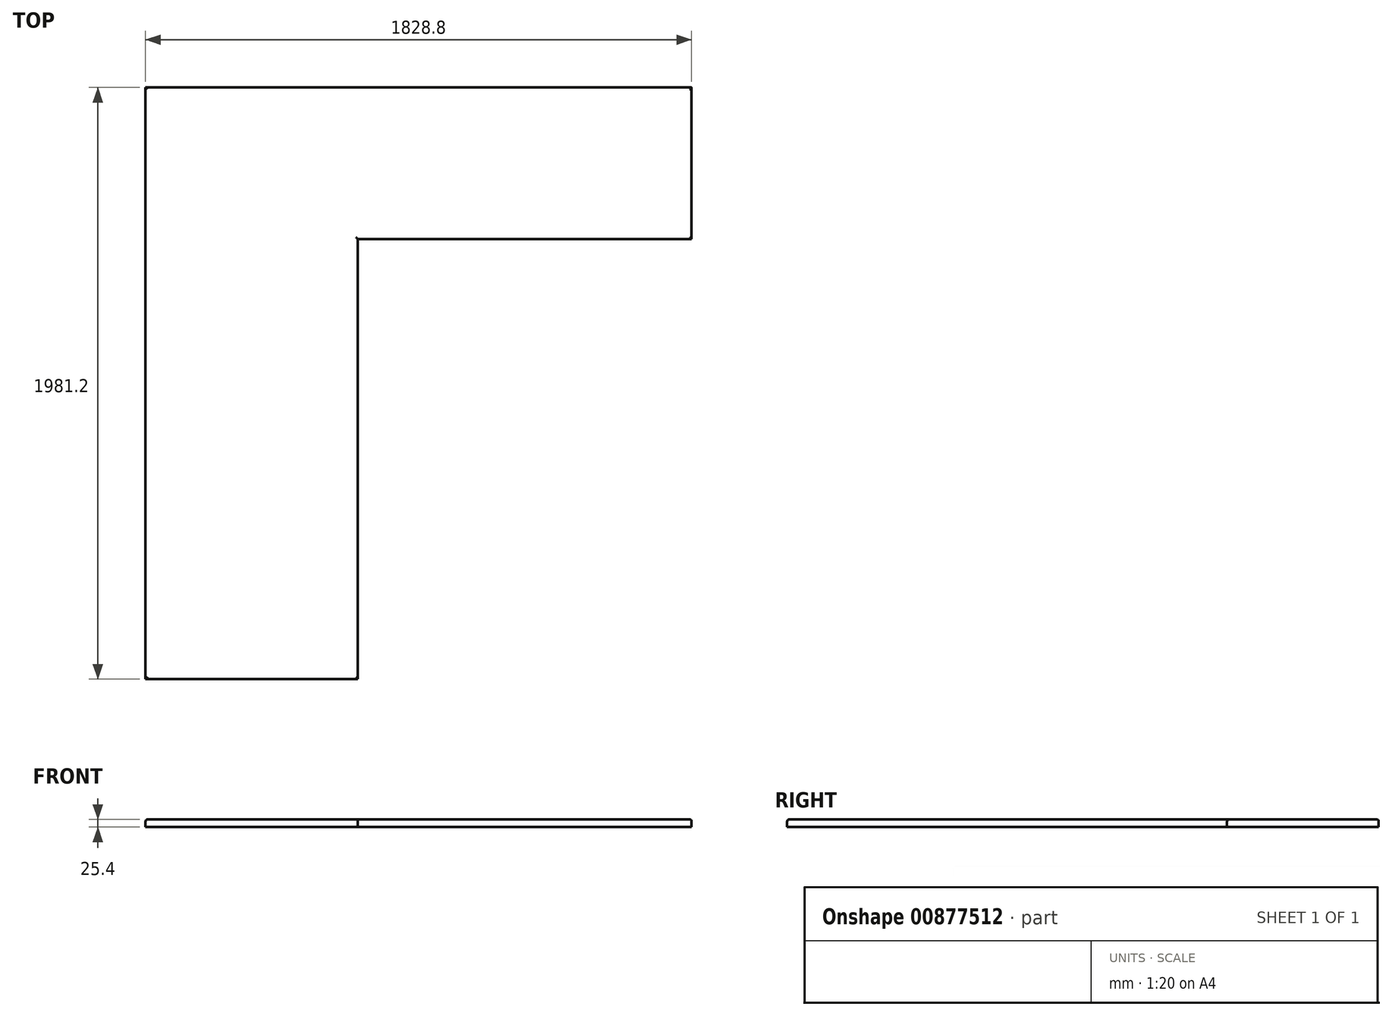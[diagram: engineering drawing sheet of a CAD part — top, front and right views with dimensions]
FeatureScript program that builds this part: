
annotation { "Feature Type Name" : "Feature", "Feature Type Description" : "" }
export const myFeature = defineFeature(function(context is Context, id is Id, definition is map)
    precondition{}
    {
        {
            var Q0;
            Q0=qCreatedBy(makeId("Top.planeOp"),FACE);
            var sketch = newSketch(context, id + "F0", { "sketchPlane" : qUnion([Q0])});
            skLineSegment(sketch, "E0", {"start": v(0, 0) * mm, "end": v(1117.6, 0) * mm});
            skLineSegment(sketch, "E1", {"start": v(1117.6, 0) * mm, "end": v(1117.6, 508) * mm});
            skLineSegment(sketch, "E2", {"start": v(1117.6, 508) * mm, "end": v(-711.2, 508) * mm});
            skLineSegment(sketch, "E3", {"start": v(-711.2, 508) * mm, "end": v(-711.2, -1473.2) * mm});
            skLineSegment(sketch, "E4", {"start": v(-711.2, -1473.2) * mm, "end": v(0, -1473.2) * mm});
            skLineSegment(sketch, "E5", {"start": v(0, -1473.2) * mm, "end": v(0, 0) * mm});
            skSolve(sketch);
        }
        {
            var Q0;
            Q0=makeQuery(id+"F0.imprint","IMPRINT",FACE,{"disambiguationData":[TD([[makeQuery(id+"F0.imprint","IMPRINT",EDGE,{"derivedFrom":sQuery(id+"F0.wireOp",EDGE,"E0")}),1.0]])]});
            extrude(context, id + "F1", {"entities" : qUnion([Q0]), "depth" : 25.4 * mm, "offsetDistance" : 25.4 * mm});
        }
        {
            var Q0;
            Q0=makeQuery(id+"F1.opExtrude","CAP_EDGE",EDGE,{"disambiguationData":[OSD([sQuery(id+"F0.wireOp",EDGE,"E5")])],"isStart":false});
            var Q1;
            Q1=makeQuery(id+"F1.opExtrude","CAP_EDGE",EDGE,{"disambiguationData":[OSD([sQuery(id+"F0.wireOp",EDGE,"E0")])],"isStart":false});
            var Q2;
            Q2=makeQuery(id+"F1.opExtrude","CAP_EDGE",EDGE,{"disambiguationData":[OSD([sQuery(id+"F0.wireOp",EDGE,"E1")])],"isStart":false});
            var Q3;
            Q3=makeQuery(id+"F1.opExtrude","CAP_EDGE",EDGE,{"disambiguationData":[OSD([sQuery(id+"F0.wireOp",EDGE,"E2")])],"isStart":false});
            var Q4;
            Q4=makeQuery(id+"F1.opExtrude","CAP_EDGE",EDGE,{"disambiguationData":[OSD([sQuery(id+"F0.wireOp",EDGE,"E3")])],"isStart":false});
            var Q5;
            Q5=makeQuery(id+"F1.opExtrude","CAP_EDGE",EDGE,{"disambiguationData":[OSD([sQuery(id+"F0.wireOp",EDGE,"E4")])],"isStart":false});
            fillet(context, id + "F2", {"entities" : qUnion([Q0, Q1, Q2, Q3, Q4, Q5]), "radius" : 6.35 * mm, "tangentPropagation" : true, "allowEdgeOverflow" : false});
        }
    });
